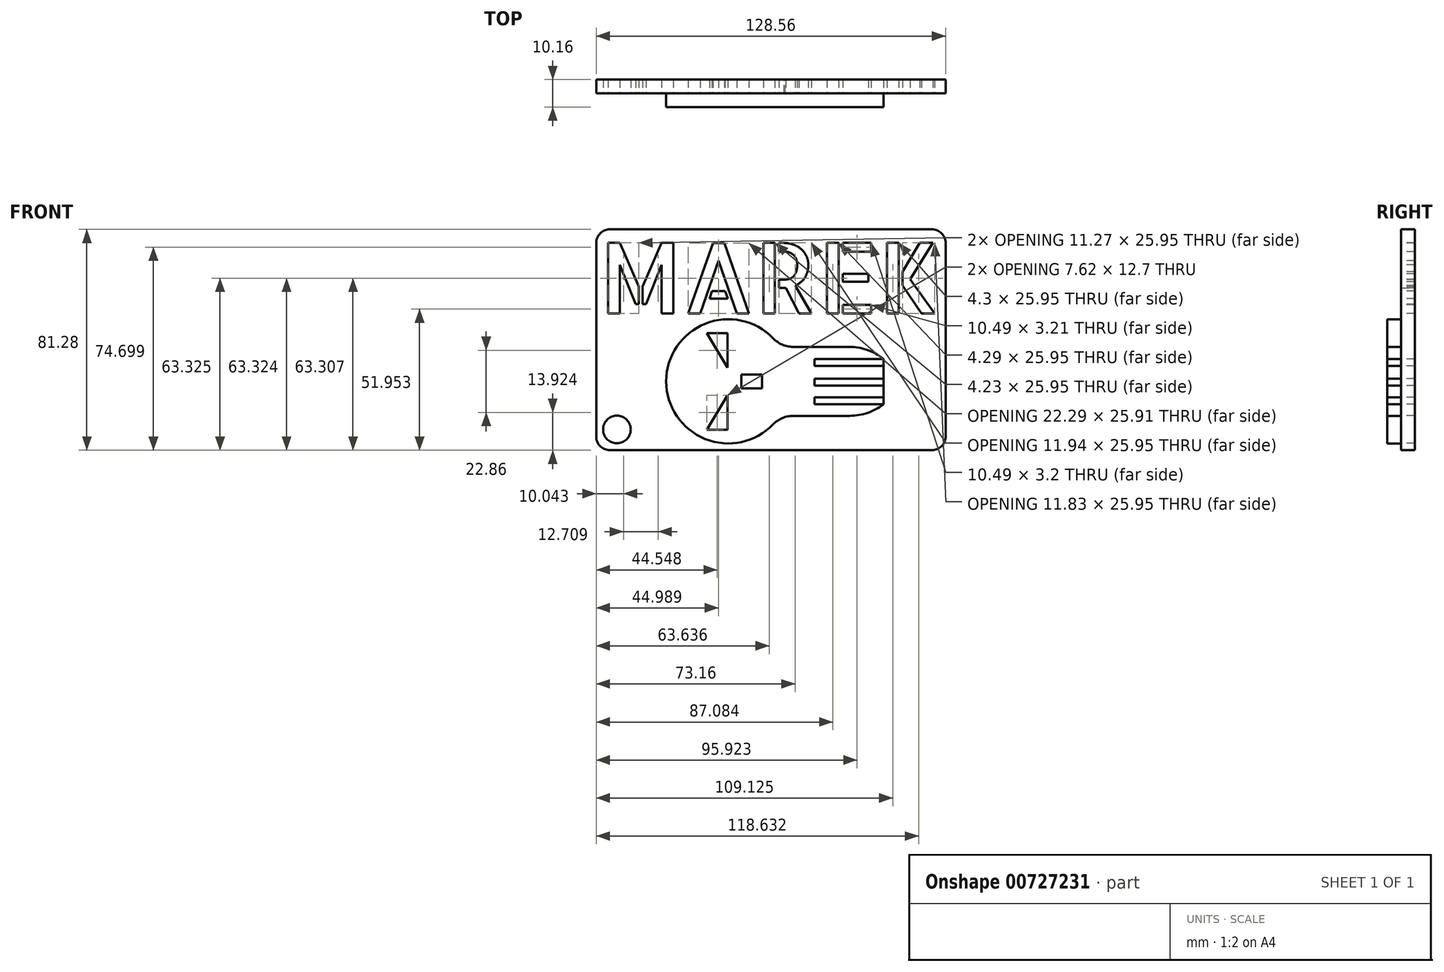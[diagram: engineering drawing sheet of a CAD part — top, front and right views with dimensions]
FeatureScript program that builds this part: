
annotation { "Feature Type Name" : "Feature", "Feature Type Description" : "" }
export const myFeature = defineFeature(function(context is Context, id is Id, definition is map)
    precondition{}
    {
        {
            var Q0;
            Q0=qCreatedBy(makeId("Front.planeOp"),FACE);
            var sketch = newSketch(context, id + "F0", { "sketchPlane" : qUnion([Q0])});
            skLineSegment(sketch, "E0.bottom", {"start": v(-72.28, 36.56) * mm, "end": v(56.28, 36.56) * mm});
            skLineSegment(sketch, "E0.top", {"start": v(-72.28, -44.72) * mm, "end": v(56.28, -44.72) * mm});
            skLineSegment(sketch, "E0.left", {"start": v(-72.28, 36.56) * mm, "end": v(-72.28, -44.72) * mm});
            skLineSegment(sketch, "E0.right", {"start": v(56.28, 36.56) * mm, "end": v(56.28, -44.72) * mm});
            skSolve(sketch);
        }
        {
            var Q0;
            Q0=makeQuery(id+"F0.imprint","IMPRINT",FACE,{"disambiguationData":[TD([[makeQuery(id+"F0.imprint","IMPRINT",EDGE,{"derivedFrom":sQuery(id+"F0.wireOp",EDGE,"E0.bottom")}),-1.0]])]});
            extrude(context, id + "F1", {"entities" : qUnion([Q0]), "depth" : 5.08 * mm, "offsetDistance" : 25.4 * mm});
        }
        {
            var Q0;
            Q0=makeQuery(id+"F1.opExtrude","CAP_FACE",FACE,{"disambiguationData":[OSD([sQuery(id+"F0.wireOp",EDGE,"E0.bottom"),sQuery(id+"F0.wireOp",EDGE,"E0.top"),sQuery(id+"F0.wireOp",EDGE,"E0.left"),sQuery(id+"F0.wireOp",EDGE,"E0.right")])],"isStart":false});
            var sketch = newSketch(context, id + "F2", { "sketchPlane" : qUnion([Q0])});
            skText(sketch, "E1", { "text": "MAREK", "fontName": "AllertaStencil-Regular.ttf"});
            const initialGuessF2  = {"E1": [-0.07111, 0.00563, 1, 0, 0.02596]};
            skSetInitialGuess(sketch, initialGuessF2);
            skSolve(sketch);
        }
        {
            var Q0;
            Q0=makeQuery(id+"F2.imprint","IMPRINT",FACE,{"disambiguationData":[TD([[makeQuery(id+"F2.imprint","IMPRINT",EDGE,{"derivedFrom":sQuery(id+"F2.wireOp",EDGE,"E1.sketch_text.stroke-0")}),1.0]])]});
            var sketch = newSketch(context, id + "F3", { "sketchPlane" : qUnion([Q0])});
            skArc(sketch, "E2", {"start": v(-4.65, -6.67) * mm, "mid": v(-46.52, -19.37) * mm, "end": v(-4.65, -32.07) * mm});
            skLineSegment(sketch, "E3.bottom", {"start": v(-4.65, -32.07) * mm, "end": v(33.45, -32.07) * mm});
            skLineSegment(sketch, "E3.top", {"start": v(-4.65, -6.67) * mm, "end": v(33.45, -6.67) * mm});
            skLineSegment(sketch, "E3.left", {"start": v(-4.65, -32.07) * mm, "end": v(-4.65, -32.07) * mm});
            skLineSegment(sketch, "E3.right", {"start": v(33.45, -32.07) * mm, "end": v(33.45, -27.79) * mm});
            skLineSegment(sketch, "E4", {"start": v(33.45, -27.79) * mm, "end": v(8.05, -27.79) * mm});
            skLineSegment(sketch, "E5", {"start": v(8.05, -27.79) * mm, "end": v(8.05, -25.25) * mm});
            skLineSegment(sketch, "E6", {"start": v(8.05, -25.25) * mm, "end": v(33.45, -25.25) * mm});
            skLineSegment(sketch, "E7", {"start": v(33.45, -11.12) * mm, "end": v(8.05, -11.12) * mm});
            skLineSegment(sketch, "E8", {"start": v(8.05, -11.12) * mm, "end": v(8.05, -13.66) * mm});
            skLineSegment(sketch, "E9", {"start": v(8.05, -13.66) * mm, "end": v(33.45, -13.66) * mm});
            skLineSegment(sketch, "E10", {"start": v(33.45, -20.88) * mm, "end": v(8.05, -20.88) * mm});
            skLineSegment(sketch, "E11", {"start": v(8.05, -20.88) * mm, "end": v(8.05, -18.34) * mm});
            skLineSegment(sketch, "E12", {"start": v(8.05, -18.34) * mm, "end": v(33.45, -18.34) * mm});
            skPoint(sketch, "E13", {"position": v(33.45, -27.79) * mm});
            skPoint(sketch, "E14", {"position": v(33.45, -25.25) * mm});
            skPoint(sketch, "E15", {"position": v(33.45, -20.88) * mm});
            skPoint(sketch, "E16", {"position": v(33.45, -18.34) * mm});
            skPoint(sketch, "E17", {"position": v(33.45, -13.66) * mm});
            skPoint(sketch, "E18", {"position": v(33.45, -11.12) * mm});
            skPoint(sketch, "E19", {"position": v(33.45, -6.67) * mm});
            skPoint(sketch, "E20", {"position": v(33.45, -32.07) * mm});
            skLineSegment(sketch, "E21.trimOffspring", {"start": v(33.45, -25.25) * mm, "end": v(33.45, -20.88) * mm});
            skLineSegment(sketch, "E22.trimOffspring", {"start": v(33.45, -18.34) * mm, "end": v(33.45, -13.66) * mm});
            skLineSegment(sketch, "E23.trimOffspring", {"start": v(33.45, -11.12) * mm, "end": v(33.45, -6.67) * mm});
            skLineSegment(sketch, "E24.trimOffspring", {"start": v(-4.65, -6.67) * mm, "end": v(-4.65, -6.67) * mm});
            skLineSegment(sketch, "E25", {"start": v(-31.54, -37.15) * mm, "end": v(-23.92, -37.15) * mm});
            skLineSegment(sketch, "E26", {"start": v(-23.92, -37.15) * mm, "end": v(-23.92, -24.45) * mm});
            skLineSegment(sketch, "E27", {"start": v(-23.92, -24.45) * mm, "end": v(-31.54, -37.15) * mm});
            skLineSegment(sketch, "E28", {"start": v(-23.92, -14.29) * mm, "end": v(-23.92, -1.59) * mm});
            skLineSegment(sketch, "E29", {"start": v(-23.92, -1.59) * mm, "end": v(-31.54, -1.59) * mm});
            skLineSegment(sketch, "E30", {"start": v(-31.54, -1.59) * mm, "end": v(-23.92, -14.29) * mm});
            skLineSegment(sketch, "E31.bottom", {"start": v(-18.88, -21.9) * mm, "end": v(-11.26, -21.9) * mm});
            skLineSegment(sketch, "E31.top", {"start": v(-18.88, -16.83) * mm, "end": v(-11.26, -16.83) * mm});
            skLineSegment(sketch, "E31.left", {"start": v(-18.88, -21.9) * mm, "end": v(-18.88, -16.83) * mm});
            skLineSegment(sketch, "E31.right", {"start": v(-11.26, -21.9) * mm, "end": v(-11.26, -16.83) * mm});
            skLineSegment(sketch, "E32", {"start": v(33.45, -27.79) * mm, "end": v(33.45, -25.25) * mm});
            skLineSegment(sketch, "E33", {"start": v(33.45, -20.88) * mm, "end": v(33.45, -18.34) * mm});
            skLineSegment(sketch, "E34", {"start": v(33.45, -13.66) * mm, "end": v(33.45, -11.12) * mm});
            skSolve(sketch);
        }
        {
            var Q0;
            Q0=makeQuery(id+"F3.imprint","IMPRINT",FACE,{"disambiguationData":[TD([[makeQuery(id+"F3.imprint","IMPRINT",EDGE,{"derivedFrom":sQuery(id+"F3.wireOp",EDGE,"E2")}),1.0]])]});
            extrude(context, id + "F4", {"entities" : qUnion([Q0]), "operationType" : NewBodyOperationType.ADD, "depth" : 5.08 * mm, "offsetDistance" : 25.4 * mm});
        }
        {
            var Q0;
            Q0 = qSketchRegion(id + "F2", true);
            extrude(context, id + "F5", {"entities" : qUnion([Q0]), "operationType" : NewBodyOperationType.REMOVE, "oppositeDirection" : true, "depth" : 25.4 * mm, "offsetDistance" : 25.4 * mm});
        }
        {
            var Q0;
            Q0=makeQuery(id+"F4.boolean.opBoolean","SPLIT",FACE,{"disambiguationData":[TD([makeQuery(id+"F4.opExtrude","SWEPT_FACE",FACE,{"disambiguationData":[OSD([sQuery(id+"F3.wireOp",EDGE,"E28")])]})])],"derivedFrom":makeQuery(id+"F1.opExtrude","CAP_FACE",FACE,{"disambiguationData":[OSD([sQuery(id+"F0.wireOp",EDGE,"E0.bottom"),sQuery(id+"F0.wireOp",EDGE,"E0.top"),sQuery(id+"F0.wireOp",EDGE,"E0.left"),sQuery(id+"F0.wireOp",EDGE,"E0.right")])],"isStart":false})});
            extrude(context, id + "F6", {"entities" : qUnion([Q0]), "operationType" : NewBodyOperationType.REMOVE, "oppositeDirection" : true, "depth" : 25.4 * mm, "offsetDistance" : 25.4 * mm});
        }
        {
            var Q0;
            Q0=makeQuery(id+"F4.boolean.opBoolean","SPLIT",FACE,{"disambiguationData":[TD([makeQuery(id+"F4.opExtrude","SWEPT_FACE",FACE,{"disambiguationData":[OSD([sQuery(id+"F3.wireOp",EDGE,"E25")])]})])],"derivedFrom":makeQuery(id+"F1.opExtrude","CAP_FACE",FACE,{"disambiguationData":[OSD([sQuery(id+"F0.wireOp",EDGE,"E0.bottom"),sQuery(id+"F0.wireOp",EDGE,"E0.top"),sQuery(id+"F0.wireOp",EDGE,"E0.left"),sQuery(id+"F0.wireOp",EDGE,"E0.right")])],"isStart":false})});
            extrude(context, id + "F7", {"entities" : qUnion([Q0]), "operationType" : NewBodyOperationType.REMOVE, "oppositeDirection" : true, "depth" : 25.4 * mm, "offsetDistance" : 25.4 * mm});
        }
        {
            var Q0;
            Q0=makeQuery(id+"F4.boolean.opBoolean","SPLIT",FACE,{"disambiguationData":[TD([makeQuery(id+"F4.opExtrude","SWEPT_FACE",FACE,{"disambiguationData":[OSD([sQuery(id+"F3.wireOp",EDGE,"E31.bottom")])]})])],"derivedFrom":makeQuery(id+"F1.opExtrude","CAP_FACE",FACE,{"disambiguationData":[OSD([sQuery(id+"F0.wireOp",EDGE,"E0.bottom"),sQuery(id+"F0.wireOp",EDGE,"E0.top"),sQuery(id+"F0.wireOp",EDGE,"E0.left"),sQuery(id+"F0.wireOp",EDGE,"E0.right")])],"isStart":false})});
            extrude(context, id + "F8", {"entities" : qUnion([Q0]), "operationType" : NewBodyOperationType.REMOVE, "oppositeDirection" : true, "depth" : 25.4 * mm, "offsetDistance" : 25.4 * mm});
        }
        {
            var Q0;
            Q0=makeQuery(id+"F3.imprint","IMPRINT",FACE,{"disambiguationData":[TD([[makeQuery(id+"F3.imprint","IMPRINT",EDGE,{"derivedFrom":sQuery(id+"F3.wireOp",EDGE,"E10")}),-1.0]])]});
            extrude(context, id + "F9", {"entities" : qUnion([Q0]), "operationType" : NewBodyOperationType.REMOVE, "oppositeDirection" : true, "depth" : 25.4 * mm, "offsetDistance" : 25.4 * mm});
        }
        {
            var Q0;
            Q0=makeQuery(id+"F3.imprint","IMPRINT",FACE,{"disambiguationData":[TD([[makeQuery(id+"F3.imprint","IMPRINT",EDGE,{"derivedFrom":sQuery(id+"F3.wireOp",EDGE,"E4")}),-1.0]])]});
            extrude(context, id + "F10", {"entities" : qUnion([Q0]), "operationType" : NewBodyOperationType.REMOVE, "oppositeDirection" : true, "depth" : 25.4 * mm, "offsetDistance" : 25.4 * mm});
        }
        {
            var Q0;
            Q0=makeQuery(id+"F3.imprint","IMPRINT",FACE,{"disambiguationData":[TD([[makeQuery(id+"F3.imprint","IMPRINT",EDGE,{"derivedFrom":sQuery(id+"F3.wireOp",EDGE,"E7")}),1.0]])]});
            extrude(context, id + "F11", {"entities" : qUnion([Q0]), "operationType" : NewBodyOperationType.REMOVE, "oppositeDirection" : true, "depth" : 25.4 * mm, "offsetDistance" : 25.4 * mm});
        }
        {
            var Q0;
            Q0=makeQuery(id+"F4.opExtrude","SWEPT_EDGE",EDGE,{"disambiguationData":[OSD([sQuery(id+"F3.wireOp",EDGE,"E2"),sQuery(id+"F3.wireOp",EDGE,"E3.bottom")])]});
            var Q1;
            Q1=makeQuery(id+"F4.opExtrude","SWEPT_EDGE",EDGE,{"disambiguationData":[OSD([sQuery(id+"F3.wireOp",EDGE,"E2"),sQuery(id+"F3.wireOp",EDGE,"E3.top")])]});
            fillet(context, id + "F12", {"entities" : qUnion([Q0, Q1]), "radius" : 10.16 * mm, "tangentPropagation" : true, "allowEdgeOverflow" : false});
        }
        {
            var Q0;
            Q0=makeQuery(id+"F4.opExtrude","SWEPT_EDGE",EDGE,{"disambiguationData":[OSD([sQuery(id+"F3.wireOp",EDGE,"E3.bottom"),sQuery(id+"F3.wireOp",EDGE,"E3.right")])]});
            var Q1;
            Q1=makeQuery(id+"F4.opExtrude","SWEPT_EDGE",EDGE,{"disambiguationData":[OSD([sQuery(id+"F3.wireOp",EDGE,"E3.top"),sQuery(id+"F3.wireOp",EDGE,"E23.trimOffspring")])]});
            fillet(context, id + "F13", {"entities" : qUnion([Q0, Q1]), "radius" : 20.32 * mm, "tangentPropagation" : true, "allowEdgeOverflow" : false});
        }
        {
            var Q0;
            Q0=makeQuery(id+"F2.imprint","IMPRINT",FACE,{"disambiguationData":[TD([[makeQuery(id+"F2.imprint","IMPRINT",EDGE,{"derivedFrom":sQuery(id+"F2.wireOp",EDGE,"E1.sketch_text.stroke-0")}),1.0]])]});
            var sketch = newSketch(context, id + "F14", { "sketchPlane" : qUnion([Q0])});
            skCircle(sketch, "E35", {"center": v(-64.66, -37.1) * mm, "radius": 5.08 * mm});
            skSolve(sketch);
        }
        {
            var Q0;
            Q0=makeQuery(id+"F14.imprint","IMPRINT",FACE,{"disambiguationData":[TD([[makeQuery(id+"F14.imprint","IMPRINT",EDGE,{"derivedFrom":sQuery(id+"F14.wireOp",EDGE,"E35")}),1.0]])]});
            extrude(context, id + "F15", {"entities" : qUnion([Q0]), "operationType" : NewBodyOperationType.REMOVE, "oppositeDirection" : true, "depth" : 25.4 * mm, "offsetDistance" : 25.4 * mm});
        }
        {
            var Q0;
            Q0=makeQuery(id+"F1.opExtrude","SWEPT_EDGE",EDGE,{"disambiguationData":[OSD([sQuery(id+"F0.wireOp",EDGE,"E0.bottom"),sQuery(id+"F0.wireOp",EDGE,"E0.right")])]});
            var Q1;
            Q1=makeQuery(id+"F1.opExtrude","SWEPT_EDGE",EDGE,{"disambiguationData":[OSD([sQuery(id+"F0.wireOp",EDGE,"E0.top"),sQuery(id+"F0.wireOp",EDGE,"E0.right")])]});
            var Q2;
            Q2=makeQuery(id+"F1.opExtrude","SWEPT_EDGE",EDGE,{"disambiguationData":[OSD([sQuery(id+"F0.wireOp",EDGE,"E0.top"),sQuery(id+"F0.wireOp",EDGE,"E0.left")])]});
            var Q3;
            Q3=makeQuery(id+"F1.opExtrude","SWEPT_EDGE",EDGE,{"disambiguationData":[OSD([sQuery(id+"F0.wireOp",EDGE,"E0.bottom"),sQuery(id+"F0.wireOp",EDGE,"E0.left")])]});
            fillet(context, id + "F16", {"entities" : qUnion([Q0, Q1, Q2, Q3]), "radius" : 5.08 * mm, "tangentPropagation" : true, "allowEdgeOverflow" : false});
        }
    });
